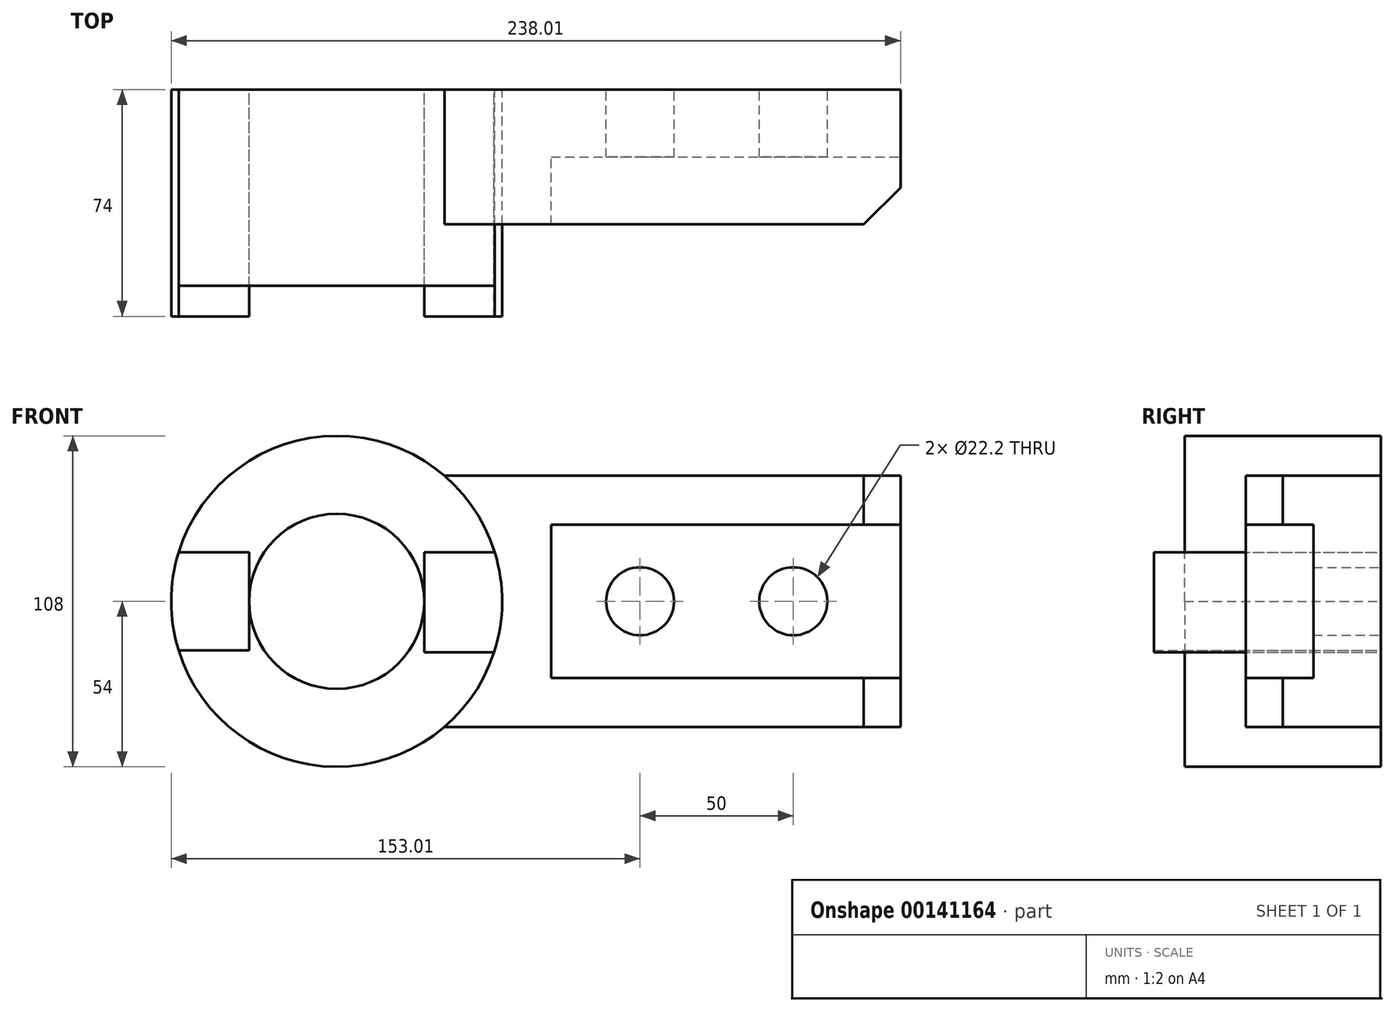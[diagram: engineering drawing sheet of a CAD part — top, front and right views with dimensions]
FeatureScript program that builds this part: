
annotation { "Feature Type Name" : "Feature", "Feature Type Description" : "" }
export const myFeature = defineFeature(function(context is Context, id is Id, definition is map)
    precondition{}
    {
        {
            var Q0;
            Q0=qCreatedBy(makeId("Front.planeOp"),FACE);
            var sketch = newSketch(context, id + "F0", { "sketchPlane" : qUnion([Q0])});
            skCircle(sketch, "E0", {"center": v(0, 0) * mm, "radius": 54 * mm});
            skLineSegment(sketch, "E1", {"start": v(70, 0) * mm, "end": v(70, 25) * mm});
            skLineSegment(sketch, "E2", {"start": v(70, 25) * mm, "end": v(184, 25) * mm});
            skLineSegment(sketch, "E3", {"start": v(70, 0) * mm, "end": v(70, -25) * mm});
            skLineSegment(sketch, "E4", {"start": v(70, -25) * mm, "end": v(184, -25) * mm});
            skLineSegment(sketch, "E5", {"start": v(184, 25) * mm, "end": v(184, 41) * mm});
            skLineSegment(sketch, "E6", {"start": v(184, 41) * mm, "end": v(35.14, 41) * mm});
            skLineSegment(sketch, "E7", {"start": v(184, -25) * mm, "end": v(184, -41) * mm});
            skLineSegment(sketch, "E8", {"start": v(184, -41) * mm, "end": v(35.14, -41) * mm});
            skLineSegment(sketch, "E9", {"start": v(184, 25) * mm, "end": v(184, -25) * mm});
            skPoint(sketch, "E10.endSnap0", {"position": v(184, 0) * mm});
            skCircle(sketch, "E11", {"center": v(149, 0) * mm, "radius": 11.1 * mm});
            skCircle(sketch, "E12", {"center": v(99, 0) * mm, "radius": 11.1 * mm});
            skCircle(sketch, "E13", {"center": v(0, 0) * mm, "radius": 28.57 * mm});
            skLineSegment(sketch, "E14", {"start": v(28.57, 0) * mm, "end": v(28.57, 16) * mm});
            skLineSegment(sketch, "E15", {"start": v(28.57, 0) * mm, "end": v(28.58, -0.62) * mm});
            skLineSegment(sketch, "E16", {"start": v(28.57, 16) * mm, "end": v(51.58, 16) * mm});
            skArc(sketch, "E17", {"start": v(54, -0.62) * mm, "mid": v(53.44, 7.78) * mm, "end": v(51.58, 16) * mm});
            skLineSegment(sketch, "E18", {"start": v(28.58, -0.62) * mm, "end": v(28.58, -16.62) * mm});
            skLineSegment(sketch, "E19", {"start": v(28.58, -16.62) * mm, "end": v(51.38, -16.62) * mm});
            skArc(sketch, "E20", {"start": v(51.38, -16.62) * mm, "mid": v(53.3, -8.72) * mm, "end": v(54, -0.62) * mm});
            skLineSegment(sketch, "E21", {"start": v(0, 0) * mm, "end": v(-28.57, 0) * mm});
            skLineSegment(sketch, "E22", {"start": v(-28.57, 0) * mm, "end": v(-28.57, 16) * mm});
            skLineSegment(sketch, "E23", {"start": v(-28.57, 0) * mm, "end": v(-28.57, -16) * mm});
            skLineSegment(sketch, "E24", {"start": v(-28.57, -16) * mm, "end": v(-51.58, -16) * mm});
            skLineSegment(sketch, "E25", {"start": v(-28.57, 16) * mm, "end": v(-51.58, 16) * mm});
            skArc(sketch, "E26", {"start": v(-51.58, 16) * mm, "mid": v(-54, 0) * mm, "end": v(-51.58, -16) * mm});
            skSolve(sketch);
        }
        {
            var Q0;
            Q0=makeQuery(id+"F0.imprint","IMPRINT",FACE,{"disambiguationData":[TD([[makeQuery(id+"F0.imprint","IMPRINT",EDGE,{"derivedFrom":sQuery(id+"F0.wireOp",EDGE,"E1")}),-1.0]])]});
            extrude(context, id + "F1", {"entities" : qUnion([Q0]), "depth" : 22 * mm});
        }
        {
            var Q0;
            Q0=makeQuery(id+"F0.imprint","IMPRINT",FACE,{"disambiguationData":[TD([[makeQuery(id+"F0.imprint","IMPRINT",EDGE,{"derivedFrom":sQuery(id+"F0.wireOp",EDGE,"E1")}),1.0]])]});
            extrude(context, id + "F2", {"entities" : qUnion([Q0]), "operationType" : NewBodyOperationType.ADD, "depth" : 44 * mm});
        }
        {
            var Q0;
            {var subQ0=sQuery(id+"F0.wireOp",EDGE,"E14");Q0=makeQuery(id+"F0.imprint","IMPRINT",FACE,{"disambiguationData":[TD([[makeQuery(id+"F0.imprint","IMPRINT",EDGE,{"derivedFrom":subQ0}),1.0]])]});}
            var Q1;
            {var subQ0=sQuery(id+"F0.wireOp",EDGE,"E15");Q1=makeQuery(id+"F0.imprint","IMPRINT",FACE,{"disambiguationData":[TD([[makeQuery(id+"F0.imprint","IMPRINT",EDGE,{"derivedFrom":subQ0}),-1.0]])]});}
            extrude(context, id + "F3", {"entities" : qUnion([Q0, Q1]), "depth" : 64 * mm});
        }
        {
            var Q0;
            Q0=makeQuery(id+"F0.imprint","IMPRINT",FACE,{"disambiguationData":[TD([[makeQuery(id+"F0.imprint","IMPRINT",EDGE,{"derivedFrom":sQuery(id+"F0.wireOp",EDGE,"E14")}),-1.0]])]});
            var Q1;
            Q1=makeQuery(id+"F0.imprint","IMPRINT",FACE,{"disambiguationData":[TD([[makeQuery(id+"F0.imprint","IMPRINT",EDGE,{"derivedFrom":sQuery(id+"F0.wireOp",EDGE,"E22")}),1.0]])]});
            extrude(context, id + "F4", {"entities" : qUnion([Q0, Q1]), "depth" : 74 * mm});
        }
        {
            var Q0;
            Q0=makeQuery(id+"F2.opExtrude","CAP_EDGE",EDGE,{"disambiguationData":[OSD([sQuery(id+"F0.wireOp",EDGE,"E5")])],"isStart":false});
            var Q1;
            Q1=makeQuery(id+"F2.opExtrude","CAP_EDGE",EDGE,{"disambiguationData":[OSD([sQuery(id+"F0.wireOp",EDGE,"E7")])],"isStart":false});
            chamfer(context, id + "F5", {"entities" : qUnion([Q0, Q1]), "width" : 12 * mm, "tangentPropagation" : true});
        }
    });
